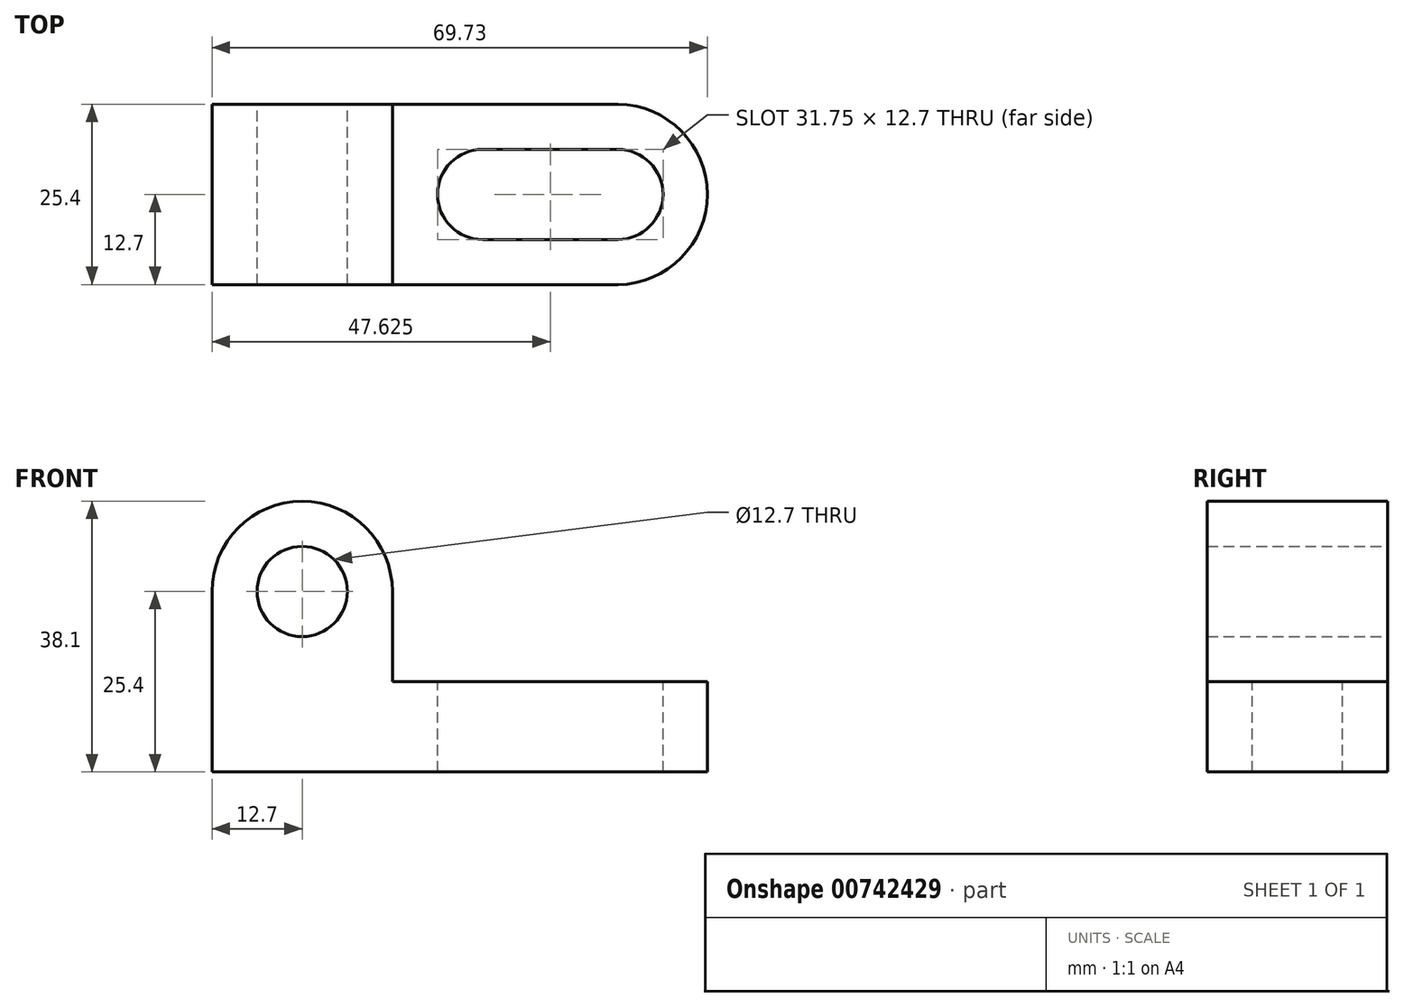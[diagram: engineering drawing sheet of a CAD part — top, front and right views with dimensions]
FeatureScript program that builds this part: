
annotation { "Feature Type Name" : "Feature", "Feature Type Description" : "" }
export const myFeature = defineFeature(function(context is Context, id is Id, definition is map)
    precondition{}
    {
        {
            var Q0;
            Q0=qCreatedBy(makeId("Front.planeOp"),FACE);
            var sketch = newSketch(context, id + "F0", { "sketchPlane" : qUnion([Q0])});
            skLineSegment(sketch, "E0", {"start": v(0, 0) * mm, "end": v(0, 38.1) * mm});
            skLineSegment(sketch, "E1", {"start": v(0, 38.1) * mm, "end": v(25.4, 38.1) * mm});
            skLineSegment(sketch, "E2", {"start": v(25.4, 38.1) * mm, "end": v(25.4, 12.7) * mm});
            skLineSegment(sketch, "E3", {"start": v(25.4, 12.7) * mm, "end": v(69.85, 12.7) * mm});
            skLineSegment(sketch, "E4", {"start": v(69.85, 12.7) * mm, "end": v(69.85, 0) * mm});
            skLineSegment(sketch, "E5", {"start": v(69.85, 0) * mm, "end": v(0, 0) * mm});
            skLineSegment(sketch, "E6", {"start": v(12.7, 38.1) * mm, "end": v(12.7, 0) * mm});
            skLineSegment(sketch, "E7", {"start": v(0, 25.4) * mm, "end": v(25.4, 25.4) * mm});
            skCircle(sketch, "E8", {"center": v(12.7, 25.4) * mm, "radius": 12.7 * mm});
            skCircle(sketch, "E9", {"center": v(12.7, 25.4) * mm, "radius": 6.35 * mm});
            skSolve(sketch);
        }
        {
            var Q0;
            Q0 = qSketchRegion(id + "F0", true);
            extrude(context, id + "F1", {"entities" : qUnion([Q0]), "depth" : 25.4 * mm, "offsetDistance" : 25.4 * mm});
        }
        {
            var Q0;
            {var subQ0=sQuery(id+"F0.wireOp",EDGE,"E1");var subQ1=sQuery(id+"F0.wireOp",EDGE,"E0");var subQ2=makeQuery(id+"F0.imprint","INTERSECT",VERTEX,{"derivedFrom":[subQ1,subQ0]});Q0=makeQuery(id+"F0.imprint","IMPRINT",FACE,{"disambiguationData":[TD([[makeQuery(id+"F0.imprint","IMPRINT",EDGE,{"disambiguationData":[TD([[subQ2,1.0]])],"derivedFrom":subQ1}),-1.0]])]});}
            var Q1;
            {var subQ0=sQuery(id+"F0.wireOp",EDGE,"E2");var subQ1=sQuery(id+"F0.wireOp",EDGE,"E1");var subQ2=makeQuery(id+"F0.imprint","INTERSECT",VERTEX,{"derivedFrom":[subQ1,subQ0]});Q1=makeQuery(id+"F0.imprint","IMPRINT",FACE,{"disambiguationData":[TD([[makeQuery(id+"F0.imprint","IMPRINT",EDGE,{"disambiguationData":[TD([[subQ2,1.0]])],"derivedFrom":subQ1}),-1.0]])]});}
            extrude(context, id + "F2", {"entities" : qUnion([Q0, Q1]), "operationType" : NewBodyOperationType.REMOVE, "depth" : 25.4 * mm, "offsetDistance" : 25.4 * mm});
        }
        {
            var Q0;
            Q0=makeQuery(id+"F1.opExtrude","SWEPT_FACE",FACE,{"disambiguationData":[OSD([sQuery(id+"F0.wireOp",EDGE,"E3")])]});
            var sketch = newSketch(context, id + "F3", { "sketchPlane" : qUnion([Q0])});
            skLineSegment(sketch, "E10", {"start": v(38.1, 0) * mm, "end": v(38.1, -25.4) * mm});
            skLineSegment(sketch, "E11", {"start": v(57.15, 0) * mm, "end": v(57.15, -25.4) * mm});
            skLineSegment(sketch, "E12", {"start": v(69.85, -12.7) * mm, "end": v(25.4, -12.7) * mm});
            skCircle(sketch, "E13", {"center": v(38.1, -12.7) * mm, "radius": 6.35 * mm});
            skCircle(sketch, "E14", {"center": v(57.15, -12.7) * mm, "radius": 6.35 * mm});
            skLineSegment(sketch, "E15", {"start": v(38.1, -6.35) * mm, "end": v(57.15, -6.35) * mm});
            skLineSegment(sketch, "E16", {"start": v(38.1, -19.05) * mm, "end": v(57.15, -19.05) * mm});
            skArc(sketch, "E17", {"start": v(57.15, -25.4) * mm, "mid": v(69.73, -12.7) * mm, "end": v(57.15, 0) * mm});
            skSolve(sketch);
        }
        {
            var Q0;
            {var subQ1=sQuery(id+"F3.wireOp",EDGE,"E10");var subQ3=sQuery(id+"F3.wireOp",EDGE,"E12");var subQ4=makeQuery(id+"F3.imprint","INTERSECT",VERTEX,{"derivedFrom":[subQ1,subQ3]});Q0=makeQuery(id+"F3.imprint","IMPRINT",FACE,{"disambiguationData":[TD([[makeQuery(id+"F3.imprint","IMPRINT",EDGE,{"disambiguationData":[TD([[subQ4,1.0]])],"derivedFrom":subQ3}),-1.0]])]});}
            var Q1;
            {var subQ1=sQuery(id+"F3.wireOp",EDGE,"E10");var subQ3=sQuery(id+"F3.wireOp",EDGE,"E12");var subQ4=makeQuery(id+"F3.imprint","INTERSECT",VERTEX,{"derivedFrom":[subQ1,subQ3]});Q1=makeQuery(id+"F3.imprint","IMPRINT",FACE,{"disambiguationData":[TD([[makeQuery(id+"F3.imprint","IMPRINT",EDGE,{"disambiguationData":[TD([[subQ4,-1.0]])],"derivedFrom":subQ3}),-1.0]])]});}
            var Q2;
            {var subQ1=sQuery(id+"F3.wireOp",EDGE,"E10");var subQ3=sQuery(id+"F3.wireOp",EDGE,"E12");var subQ4=makeQuery(id+"F3.imprint","INTERSECT",VERTEX,{"derivedFrom":[subQ1,subQ3]});Q2=makeQuery(id+"F3.imprint","IMPRINT",FACE,{"disambiguationData":[TD([[makeQuery(id+"F3.imprint","IMPRINT",EDGE,{"disambiguationData":[TD([[subQ4,1.0]])],"derivedFrom":subQ3}),1.0]])]});}
            var Q3;
            {var subQ1=sQuery(id+"F3.wireOp",EDGE,"E10");var subQ3=sQuery(id+"F3.wireOp",EDGE,"E12");var subQ4=makeQuery(id+"F3.imprint","INTERSECT",VERTEX,{"derivedFrom":[subQ1,subQ3]});Q3=makeQuery(id+"F3.imprint","IMPRINT",FACE,{"disambiguationData":[TD([[makeQuery(id+"F3.imprint","IMPRINT",EDGE,{"disambiguationData":[TD([[subQ4,-1.0]])],"derivedFrom":subQ3}),1.0]])]});}
            var Q4;
            {var subQ1=sQuery(id+"F3.wireOp",EDGE,"E11");var subQ3=sQuery(id+"F3.wireOp",EDGE,"E12");var subQ4=makeQuery(id+"F3.imprint","INTERSECT",VERTEX,{"derivedFrom":[subQ1,subQ3]});Q4=makeQuery(id+"F3.imprint","IMPRINT",FACE,{"disambiguationData":[TD([[makeQuery(id+"F3.imprint","IMPRINT",EDGE,{"disambiguationData":[TD([[subQ4,1.0]])],"derivedFrom":subQ3}),-1.0]])]});}
            var Q5;
            {var subQ1=sQuery(id+"F3.wireOp",EDGE,"E11");var subQ3=sQuery(id+"F3.wireOp",EDGE,"E12");var subQ4=makeQuery(id+"F3.imprint","INTERSECT",VERTEX,{"derivedFrom":[subQ1,subQ3]});Q5=makeQuery(id+"F3.imprint","IMPRINT",FACE,{"disambiguationData":[TD([[makeQuery(id+"F3.imprint","IMPRINT",EDGE,{"disambiguationData":[TD([[subQ4,-1.0]])],"derivedFrom":subQ3}),-1.0]])]});}
            var Q6;
            {var subQ1=sQuery(id+"F3.wireOp",EDGE,"E11");var subQ3=sQuery(id+"F3.wireOp",EDGE,"E12");var subQ4=makeQuery(id+"F3.imprint","INTERSECT",VERTEX,{"derivedFrom":[subQ1,subQ3]});Q6=makeQuery(id+"F3.imprint","IMPRINT",FACE,{"disambiguationData":[TD([[makeQuery(id+"F3.imprint","IMPRINT",EDGE,{"disambiguationData":[TD([[subQ4,1.0]])],"derivedFrom":subQ3}),1.0]])]});}
            var Q7;
            {var subQ1=sQuery(id+"F3.wireOp",EDGE,"E11");var subQ3=sQuery(id+"F3.wireOp",EDGE,"E12");var subQ4=makeQuery(id+"F3.imprint","INTERSECT",VERTEX,{"derivedFrom":[subQ1,subQ3]});Q7=makeQuery(id+"F3.imprint","IMPRINT",FACE,{"disambiguationData":[TD([[makeQuery(id+"F3.imprint","IMPRINT",EDGE,{"disambiguationData":[TD([[subQ4,-1.0]])],"derivedFrom":subQ3}),1.0]])]});}
            var Q8;
            {var subQ5=sQuery(id+"F3.wireOp",EDGE,"E15");Q8=makeQuery(id+"F3.imprint","IMPRINT",FACE,{"disambiguationData":[TD([[makeQuery(id+"F3.imprint","IMPRINT",EDGE,{"derivedFrom":subQ5}),-1.0]])]});}
            var Q9;
            {var subQ5=sQuery(id+"F3.wireOp",EDGE,"E16");Q9=makeQuery(id+"F3.imprint","IMPRINT",FACE,{"disambiguationData":[TD([[makeQuery(id+"F3.imprint","IMPRINT",EDGE,{"derivedFrom":subQ5}),1.0]])]});}
            var Q10;
            {var subQ0=sQuery(id+"F3.wireOp",EDGE,"E12");var subQ4=sQuery(id+"F3.wireOp",EDGE,"E17");var subQ5=makeQuery(id+"F3.imprint","INTERSECT",VERTEX,{"derivedFrom":[subQ0,subQ4]});Q10=makeQuery(id+"F3.imprint","IMPRINT",FACE,{"disambiguationData":[TD([[makeQuery(id+"F3.imprint","IMPRINT",EDGE,{"disambiguationData":[TD([[subQ5,1.0]])],"derivedFrom":subQ0}),1.0]])]});}
            var Q11;
            {var subQ0=sQuery(id+"F3.wireOp",EDGE,"E12");var subQ4=sQuery(id+"F3.wireOp",EDGE,"E17");var subQ5=makeQuery(id+"F3.imprint","INTERSECT",VERTEX,{"derivedFrom":[subQ0,subQ4]});Q11=makeQuery(id+"F3.imprint","IMPRINT",FACE,{"disambiguationData":[TD([[makeQuery(id+"F3.imprint","IMPRINT",EDGE,{"disambiguationData":[TD([[subQ5,1.0]])],"derivedFrom":subQ0}),-1.0]])]});}
            extrude(context, id + "F4", {"entities" : qUnion([Q0, Q1, Q2, Q3, Q4, Q5, Q6, Q7, Q8, Q9, Q10, Q11]), "operationType" : NewBodyOperationType.REMOVE, "oppositeDirection" : true, "depth" : 25.4 * mm, "offsetDistance" : 25.4 * mm});
        }
    });
